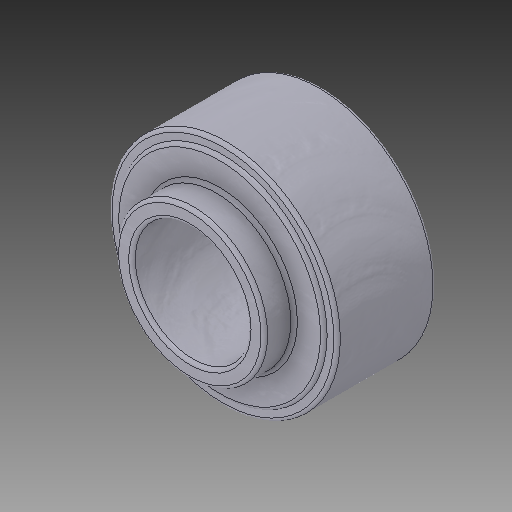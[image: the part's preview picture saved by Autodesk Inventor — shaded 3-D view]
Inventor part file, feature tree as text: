
AUTODESK INVENTOR PART (.ipt)
format: ipt  version: 2019 (Build 230136000, 136)  size: 220,672 bytes
history: native  units: in
note: dims shown in document units (in); Inventor stores cm internally (conversion verified against a paired STEP export)
features: sketch x6, other x3
ambient origin geometry x8: Origin, YZ Plane, XZ Plane, XY Plane, X Axis, Y Axis, Z Axis, Center Point
bodies: Solid1 (feature_tree)
feature tree (9):
  other  "project flange bearing part2_MIR4.ipt"
  other  "Solid1::project flange bearing part2_MIR4.ipt"
  other  "TaggingFeature1"
  sketch  "Sketch1"  dims[d0=0.3937in]
  sketch  "Sketch2"
  sketch  "Sketch3"
  sketch  "Sketch4"
  sketch  "Sketch5"
  sketch  "Sketch6"
